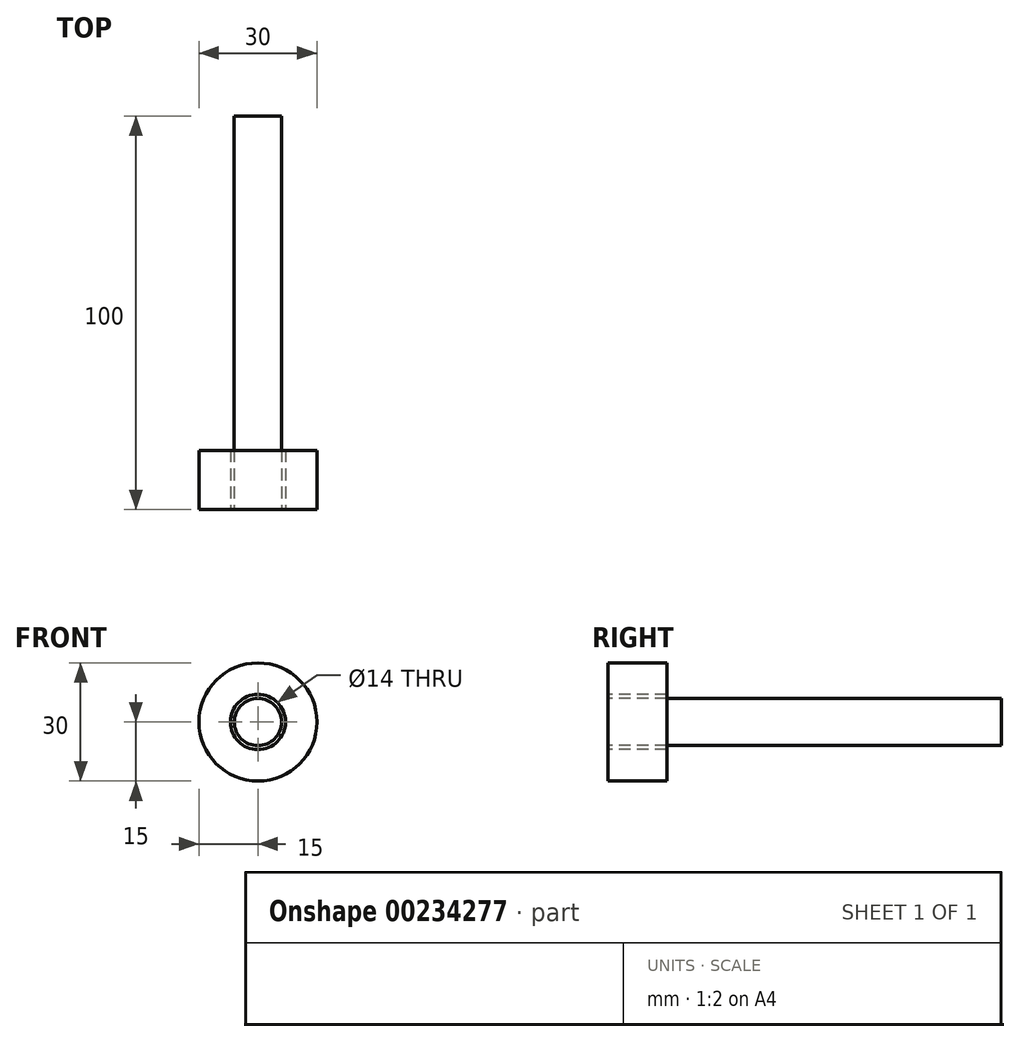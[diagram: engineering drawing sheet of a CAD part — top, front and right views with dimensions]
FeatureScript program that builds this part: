
annotation { "Feature Type Name" : "Feature", "Feature Type Description" : "" }
export const myFeature = defineFeature(function(context is Context, id is Id, definition is map)
    precondition{}
    {
        {
            var Q0;
            Q0=qCreatedBy(makeId("Front.planeOp"),FACE);
            var sketch = newSketch(context, id + "F0", { "sketchPlane" : qUnion([Q0])});
            skCircle(sketch, "E0", {"center": v(0, 0) * mm, "radius": 6 * mm});
            skSolve(sketch);
        }
        {
            var Q0;
            Q0 = qSketchRegion(id + "F0", true);
            extrude(context, id + "F1", {"entities" : qUnion([Q0]), "oppositeDirection" : true, "depth" : 100 * mm, "offsetDistance" : 25 * mm});
        }
        {
            var Q0;
            Q0=makeQuery(id+"F1.opExtrude","CAP_FACE",FACE,{"disambiguationData":[OSD([sQuery(id+"F0.wireOp",EDGE,"E0")])],"isStart":true});
            var sketch = newSketch(context, id + "F2", { "sketchPlane" : qUnion([Q0])});
            skCircle(sketch, "E1", {"center": v(0, 0) * mm, "radius": 15 * mm});
            skCircle(sketch, "E2", {"center": v(0, 0) * mm, "radius": 7 * mm});
            skSolve(sketch);
        }
        {
            var Q0;
            Q0=makeQuery(id+"F2.imprint","IMPRINT",FACE,{"disambiguationData":[TD([[makeQuery(id+"F2.imprint","IMPRINT",EDGE,{"derivedFrom":sQuery(id+"F2.wireOp",EDGE,"E1")}),1.0]])]});
            extrude(context, id + "F3", {"entities" : qUnion([Q0]), "oppositeDirection" : true, "depth" : 15 * mm, "offsetDistance" : 25 * mm});
        }
    });
